# Revit family: Точечный зенитный фонарь (люк) M8CITY_П
name_source: partatom
category: Окна
revit_build: Autodesk Revit 2017 (Build: 20170118_1100(x64)
units: mm (PartAtom-declared; Revit-internal decimal feet)

## family parameters
Всегда вертикально = Нет
Общий = Нет
Основа = Крыша
При загрузке вырезать с полостями = Нет
Точка расчета площади = Нет

## types (1)
- Зенитный фонарь M8CITY Т-П-pro
    URL = www.m8city.by
    Высота = 600 мм
    Высота основания = 527 мм
    Длина = 1400 мм
    Длина проёма = 1400 мм
    Длина проёма ввод = 1400 мм
    Изготовитель = ООО Завод М8 Сити Про
    Описание = Точечный зенитный фонарь (люк) M8CITY pro с алюминиевым обрамлением сложного сечения
    ПМ16 = Купол зенитного фонаря П pro : ПК молочный 16 мм
    ПМ20 = Купол зенитного фонаря П pro : ПК молочный 20 мм
    ПП16 = Купол зенитного фонаря П pro : ПК прозрачный 16 мм
    ПП20 = Купол зенитного фонаря П pro : ПК прозрачный 20 мм
    СП24 = Купол зенитного фонаря П pro : СП 24 мм
    СП26 = Купол зенитного фонаря П pro : СП 26 мм
    СПЛ25 = Купол зенитного фонаря П pro : Сендвич-панель 25 мм
    Ширина = 1600 мм
    Ширина проёма = 1600 мм
    Ширина проёма ввод = 1600 мм
